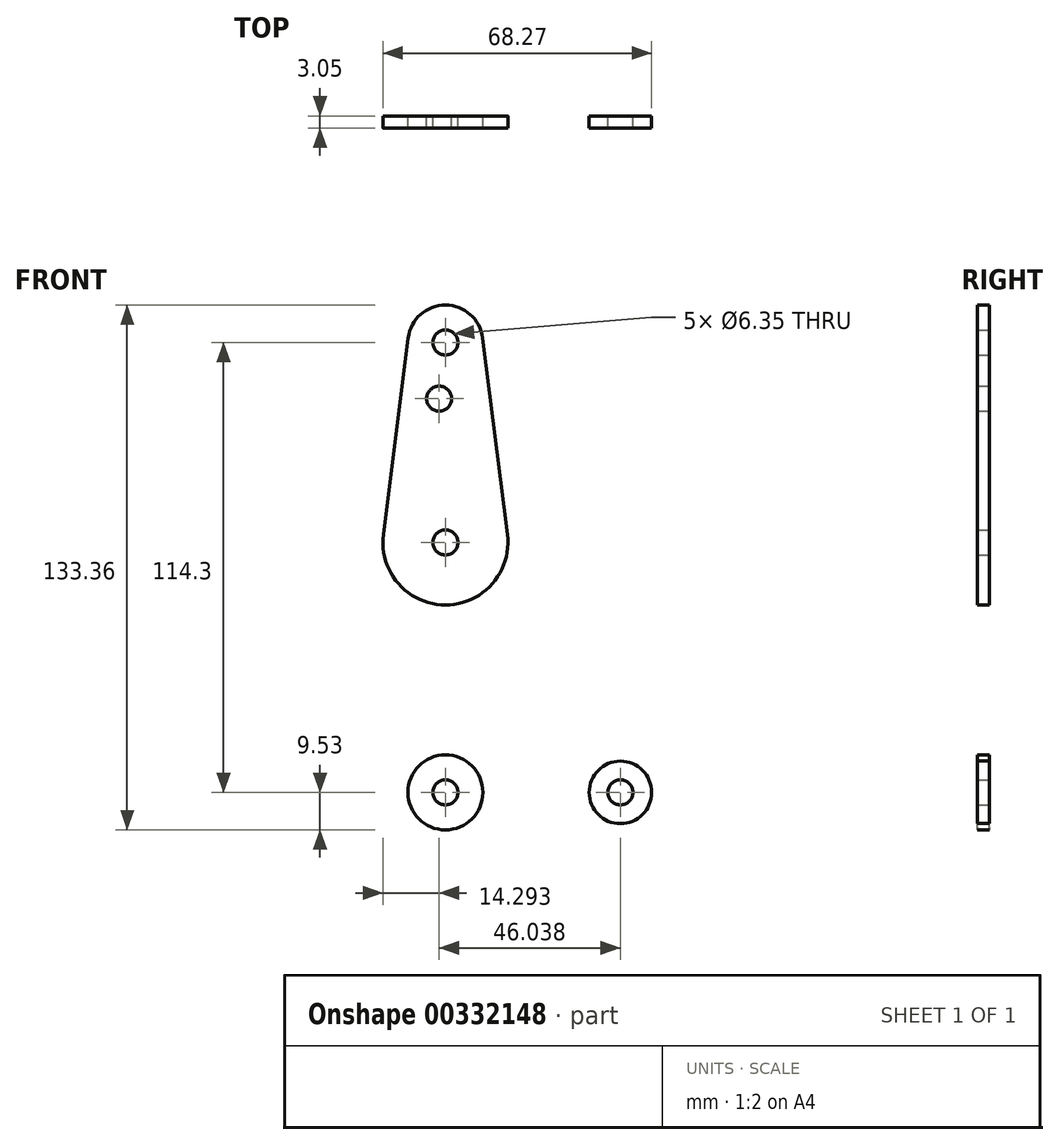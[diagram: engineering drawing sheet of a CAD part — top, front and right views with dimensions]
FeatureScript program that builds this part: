
annotation { "Feature Type Name" : "Feature", "Feature Type Description" : "" }
export const myFeature = defineFeature(function(context is Context, id is Id, definition is map)
    precondition{}
    {
        {
            var Q0;
            Q0=qCreatedBy(makeId("Front.planeOp"),FACE);
            var sketch = newSketch(context, id + "F0", { "sketchPlane" : qUnion([Q0])});
            skCircle(sketch, "E0", {"center": v(0, 0) * mm, "radius": 9.53 * mm});
            skLineSegment(sketch, "E1", {"start": v(0, 0) * mm, "end": v(0, 114.3) * mm, "construction": true});
            skCircle(sketch, "E2", {"center": v(0, 114.3) * mm, "radius": 9.53 * mm});
            skLineSegment(sketch, "E3", {"start": v(0, 0) * mm, "end": v(44.45, 0) * mm, "construction": true});
            skCircle(sketch, "E4", {"center": v(44.45, 0) * mm, "radius": 7.94 * mm});
            skCircle(sketch, "E5", {"center": v(0, 63.5) * mm, "radius": 15.88 * mm});
            skLineSegment(sketch, "E6", {"start": v(-9.45, 115.5) * mm, "end": v(-15.75, 65.48) * mm});
            skLineSegment(sketch, "E7", {"start": v(9.45, 115.5) * mm, "end": v(15.75, 65.48) * mm});
            skCircle(sketch, "E8", {"center": v(0, 114.3) * mm, "radius": 3.18 * mm});
            skCircle(sketch, "E9", {"center": v(-1.59, 100.03) * mm, "radius": 3.18 * mm});
            skCircle(sketch, "E10", {"center": v(0, 63.5) * mm, "radius": 3.18 * mm});
            skCircle(sketch, "E11", {"center": v(0, 0) * mm, "radius": 3.18 * mm});
            skCircle(sketch, "E12", {"center": v(44.45, 0) * mm, "radius": 3.18 * mm});
            skPoint(sketch, "E13.newPointB", {"position": v(-0.03, 0) * mm});
            skLineSegment(sketch, "E14", {"start": v(15.87, 63.5) * mm, "end": v(15.88, 15.85) * mm});
            skArc(sketch, "E15.filletArc", {"start": v(15.88, 15.85) * mm, "mid": v(18.5, 9.95) * mm, "end": v(24.62, 7.94) * mm});
            skLineSegment(sketch, "E16", {"start": v(44.45, 7.94) * mm, "end": v(24.62, 7.94) * mm});
            skLineSegment(sketch, "E17", {"start": v(0, -9.52) * mm, "end": v(44.45, -7.94) * mm});
            skLineSegment(sketch, "E18", {"start": v(-15.75, 65.48) * mm, "end": v(-9.57, 0) * mm});
            skSolve(sketch);
        }
        {
            var Q0;
            Q0 = qSketchRegion(id + "F0", true);
            extrude(context, id + "F1", {"entities" : qUnion([Q0]), "depth" : 3.05 * mm});
        }
    });
